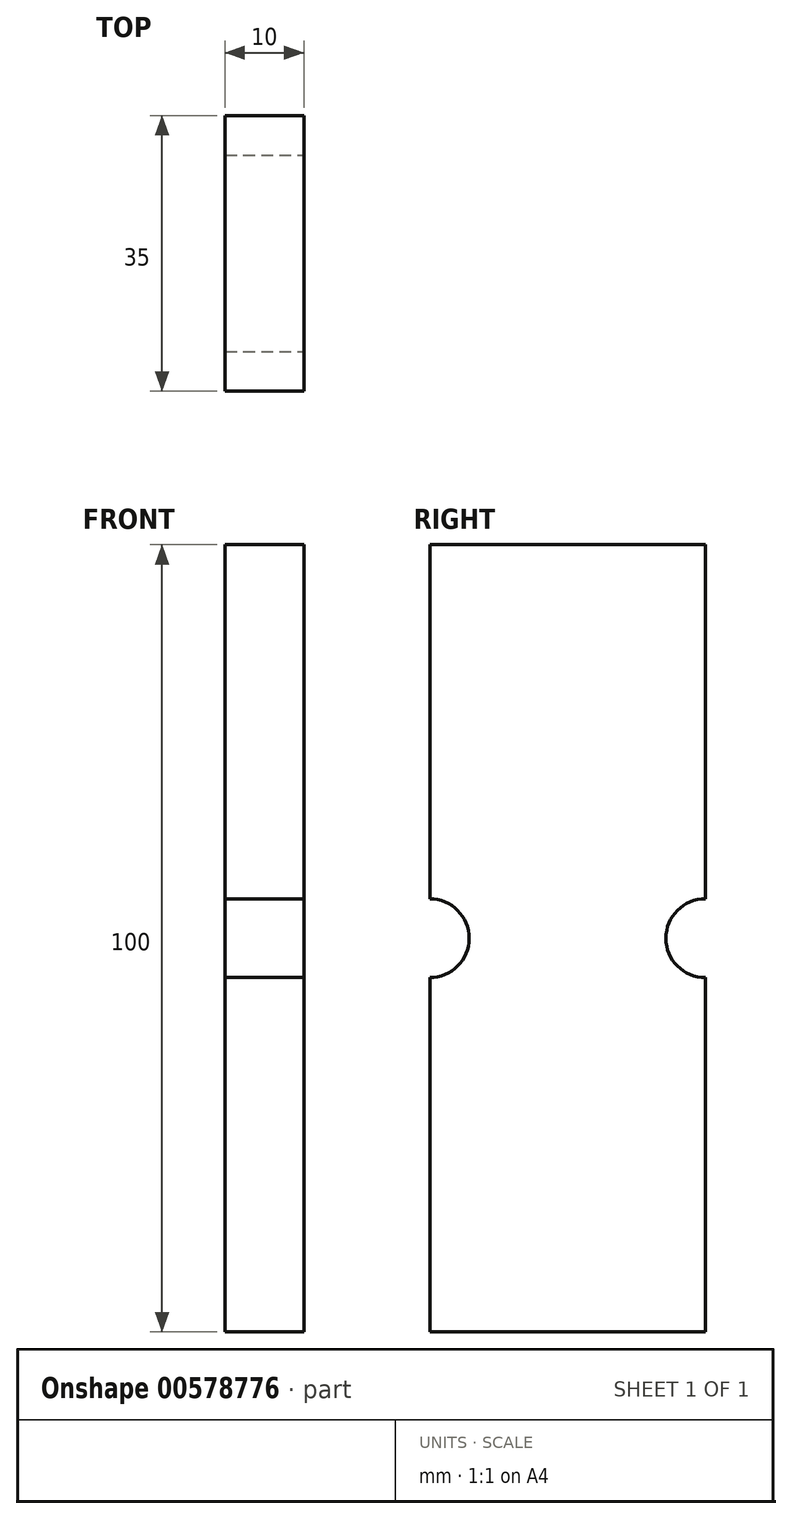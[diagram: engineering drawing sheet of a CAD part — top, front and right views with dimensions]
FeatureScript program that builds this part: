
annotation { "Feature Type Name" : "Feature", "Feature Type Description" : "" }
export const myFeature = defineFeature(function(context is Context, id is Id, definition is map)
    precondition{}
    {
        {
            var Q0;
            Q0=qCreatedBy(makeId("Right.planeOp"),FACE);
            var sketch = newSketch(context, id + "F0", { "sketchPlane" : qUnion([Q0])});
            skLineSegment(sketch, "E0.bottom", {"start": v(-17.5, 50) * mm, "end": v(17.5, 50) * mm});
            skLineSegment(sketch, "E0.top", {"start": v(-17.5, -50) * mm, "end": v(17.5, -50) * mm});
            skLineSegment(sketch, "E0.left", {"start": v(-17.5, 50) * mm, "end": v(-17.5, -50) * mm});
            skLineSegment(sketch, "E0.right", {"start": v(17.5, 50) * mm, "end": v(17.5, -50) * mm});
            skSolve(sketch);
        }
        {
            var Q0;
            Q0 = qSketchRegion(id + "F0", true);
            extrude(context, id + "F1", {"entities" : qUnion([Q0]), "depth" : 5 * mm, "offsetDistance" : 25 * mm, "hasSecondDirection" : true, "secondDirectionOppositeDirection" : true, "secondDirectionDepth" : 5 * mm});
        }
        {
            var Q0;
            Q0=qCreatedBy(makeId("Right.planeOp"),FACE);
            var sketch = newSketch(context, id + "F2", { "sketchPlane" : qUnion([Q0])});
            skCircle(sketch, "E1", {"center": v(-17.5, 0) * mm, "radius": 5 * mm});
            skCircle(sketch, "E2", {"center": v(17.5, 0) * mm, "radius": 5 * mm});
            skSolve(sketch);
        }
        {
            var Q0;
            Q0 = qSketchRegion(id + "F2", true);
            extrude(context, id + "F3", {"entities" : qUnion([Q0]), "operationType" : NewBodyOperationType.REMOVE, "oppositeDirection" : true, "depth" : 25 * mm, "offsetDistance" : 25 * mm, "hasSecondDirection" : true, "secondDirectionOppositeDirection" : false, "secondDirectionDepth" : 25 * mm});
        }
    });
